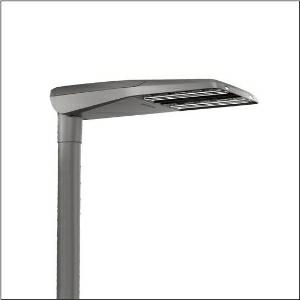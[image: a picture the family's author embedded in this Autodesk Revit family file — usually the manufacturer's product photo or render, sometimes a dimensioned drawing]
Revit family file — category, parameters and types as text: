
# Revit family: streetlight_sl_11_iq_midi___st1_2p1_0_5xc3g51f08me_c537
name_source: partatom
category: Lighting Fixtures
units: mm (PartAtom-declared; Revit-internal decimal feet)

## family parameters
Cut with Voids When Loaded = No
Host = Face
Light Source = No
Part Type = Normal
Room Calculation Point = No
Round Connector Dimension = Use Diameter
Shared = No

## types (1)
- --- (1 x LED, 17750 lm, 121.7 W, 3000K)
    Apparent Load = 122 VA
    CIE Flux Codes = 31 68 95 100 100
    Color Rendering = 70
    Color Temperature = 3000K
    Default Elevation = 1800 mm
    Description = Streetlight SL 11 iQ midi, mast luminaire, primary light control with 3 zone facetted reflector, of plastic, silver coated, highly specular, primary optical cover: cover, of PMMA, transparent, light distribution: ST1.2P1.0, light emission: direct distribution, primary light characteristic: asymmetric, installation type: post-top, side-entry, lamps: LED, High Power LED, rated values: 17.750lm | 121,7W | 145,9lm/W (begin service life); end service life: 17.750lm | 129W; at 50% lumin. flux: 8.875lm | 56W | 158,5lm/W, colour temperature: 3000K, colour rendering: CRI > 70, light colour: 730, light setting 1 begin service life: 100% | 17.750lm | 121,7W | 145,9lm/W | 3.000K, light setting 1 end service life: 129W, further light settings possible, control: Street-Remote, optimised constant luminous flux control (CLO 2.0), Auto-Match, Desk-Remote (wireless, voltage-free reading and setting of iQ features in the workshop via application-optimized NFC function/RFID function), Light-Fading, Smart-Wire, Night-Set, Lumen-Switch, Temp-Guard, with cable H07RN-F 5x 1.5mm², mains connection: 230..240V, AC, 50/60Hz, connection cable pre-assembled, cable length: 12,5m, luminaire housing, of diecast aluminium, powder-coated, Siteco® metallic grey (DB 702S), please order mast flange separately, inclination adjustable without tools: 0°, 5°, 10°, 15° (post-top) | 0°, -5°, -10°, -15° (side-entry), sealing non-destructively replaceable, multi-level sealing system, length: 780mm, width: 376mm, height: 118mm, mast flange for spigot size: 42mm (side-entry): 5XC10008XM4, 60/48mm (side-entry/post-top): 5XC10108XM2, 76/60mm (side-entry/post-top): 5XC10108XM1, equipment: Power, protection rating (complete): IP66, insulation class (complete): insulation class II (safety insulation), certification: CE, ENEC, ENEC+, VDE, impact resistance: IK10, permissible operating ambient temperature for outdoor applications: -25..+50°C, standard-compliant lighting for roads and squares, Environmental Product Declaration (EPD) tested and certified by an independent institute, packaging unit: 1 piece

Light Distribution: ST1.2P1.0
    Height = 118 mm
    Lamp = 1 x LED
    Lamp Light Flux = 17750 lm
    Lamp Power = 121.7 W
    Lamp count = 1
    Length = 780 mm
    Luminous efficacy = 146 lm/W
    Manufacturer = Siteco
    ModVariant = No
    Model = 5XC3G51F08ME
    Number of Poles = 1
    OnlyDefault = Yes
    Power Factor = 1
    Product Name = Streetlight SL 11 iQ midi | ST1.2P1.0
    Product group = mast luminaire | pylon top
    ProductGroupID = 6100
    Protection Class = Protection class II
    Protection Degree = IP 66
    RLX_Detail_Level = 1
    RLX_Emergency_Light_Flux = 0 lm
    RLX_Emergency_Type = 0
    RLX_Emergency_Type_DB = No
    RlxData = <blob elided: 70929 chars, md5=d6da59ec>
    Socket = socket
    Standby Power = 0 W
    System Light Flux = 17750 lm
    System Power = 122 W
    Type Comments = factory setting: luminous flux: 100 % | dim-lin: 254 | 544 mA
    Type Image = l_1005960.jpg
    URL = http://relux.com
    VarID = @adj_057529
    Voltage = 0 V
    Weight = 0.00 kg
    Width = 376 mm

## geometry (parser evidence)
native form markers: Blend x4, Sweep x9
no freeform markers — native parametric forms only
